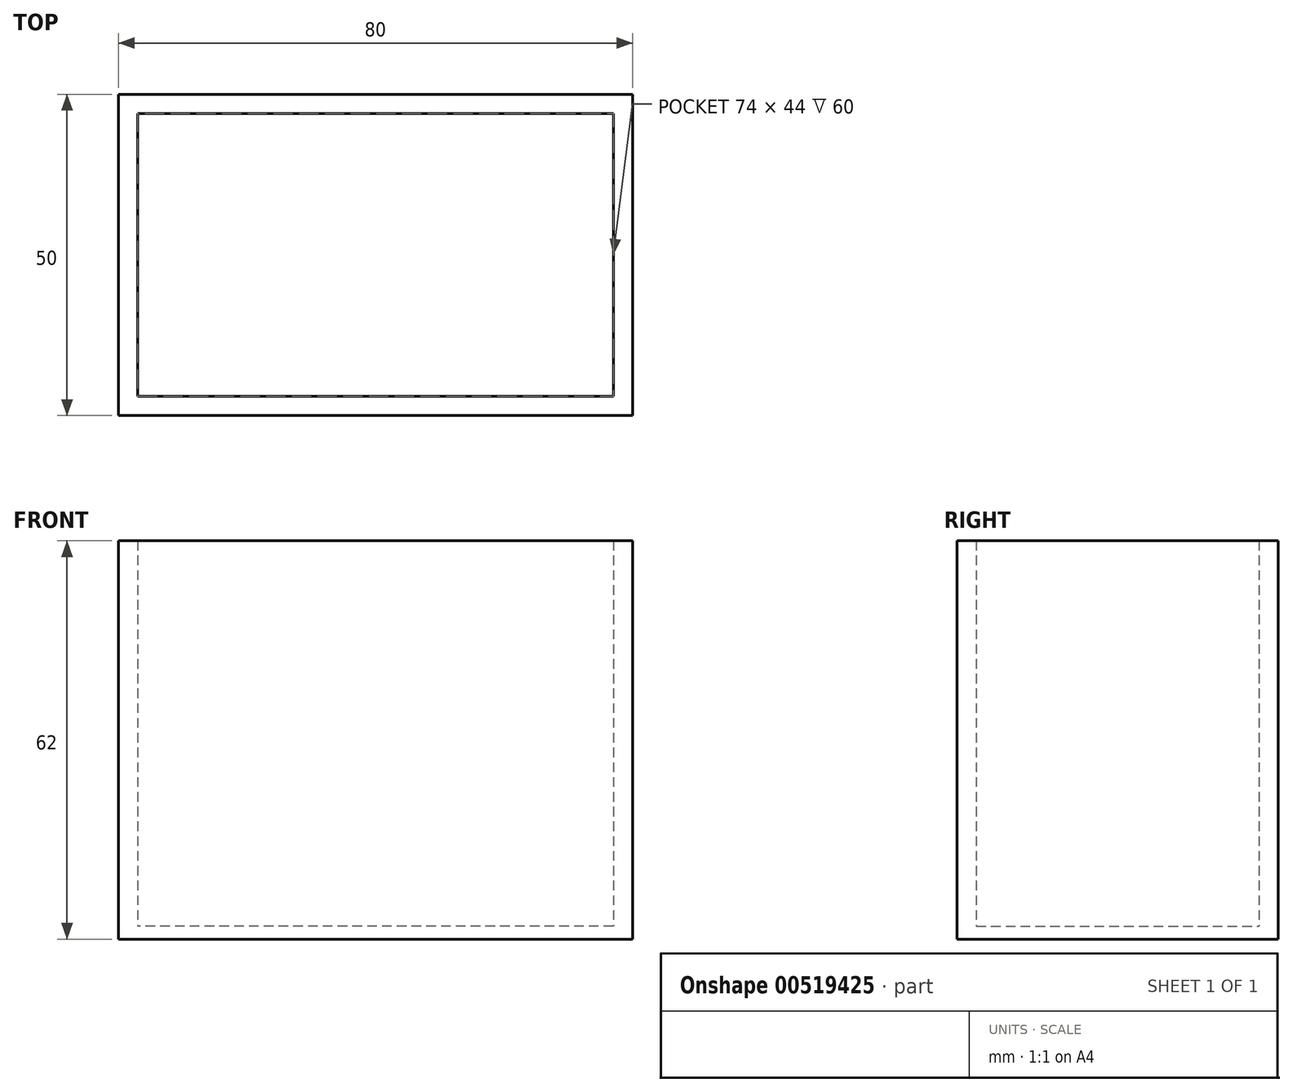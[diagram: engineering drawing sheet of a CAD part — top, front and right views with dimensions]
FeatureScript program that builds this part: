
annotation { "Feature Type Name" : "Feature", "Feature Type Description" : "" }
export const myFeature = defineFeature(function(context is Context, id is Id, definition is map)
    precondition{}
    {
        {
            var Q0;
            Q0=qCreatedBy(makeId("Top.planeOp"),FACE);
            var sketch = newSketch(context, id + "F0", { "sketchPlane" : qUnion([Q0])});
            skLineSegment(sketch, "E0.bottom", {"start": v(40, -25) * mm, "end": v(-40, -25) * mm});
            skLineSegment(sketch, "E0.top", {"start": v(40, 25) * mm, "end": v(-40, 25) * mm});
            skLineSegment(sketch, "E0.left", {"start": v(40, -25) * mm, "end": v(40, 25) * mm});
            skLineSegment(sketch, "E0.right", {"start": v(-40, -25) * mm, "end": v(-40, 25) * mm});
            skPoint(sketch, "E0.middle", {"position": v(0, 0) * mm});
            skSolve(sketch);
        }
        {
            var Q0;
            Q0 = qSketchRegion(id + "F0", true);
            var Q1;
            Q1=makeQuery(id+"F0.imprint","IMPRINT",FACE,{"disambiguationData":[TD([[makeQuery(id+"F0.imprint","IMPRINT",EDGE,{"derivedFrom":sQuery(id+"F0.wireOp",EDGE,"E0.bottom")}),-1.0]])]});
            extrude(context, id + "F1", {"entities" : qUnion([Q0, Q1]), "depth" : 2 * mm, "offsetDistance" : 25 * mm});
        }
        {
            var Q0;
            Q0=makeQuery(id+"F1.opExtrude","CAP_FACE",FACE,{"disambiguationData":[OSD([sQuery(id+"F0.wireOp",EDGE,"E0.bottom"),sQuery(id+"F0.wireOp",EDGE,"E0.top"),sQuery(id+"F0.wireOp",EDGE,"E0.left"),sQuery(id+"F0.wireOp",EDGE,"E0.right")])],"isStart":false});
            var sketch = newSketch(context, id + "F2", { "sketchPlane" : qUnion([Q0])});
            skLineSegment(sketch, "E1.bottom", {"start": v(37, -22) * mm, "end": v(-37, -22) * mm});
            skLineSegment(sketch, "E1.top", {"start": v(37, 22) * mm, "end": v(-37, 22) * mm});
            skLineSegment(sketch, "E1.left", {"start": v(37, -22) * mm, "end": v(37, 22) * mm});
            skLineSegment(sketch, "E1.right", {"start": v(-37, -22) * mm, "end": v(-37, 22) * mm});
            skPoint(sketch, "E1.middle", {"position": v(0, 0) * mm});
            skLineSegment(sketch, "E2.bottom", {"start": v(-40, 25) * mm, "end": v(40, 25) * mm});
            skLineSegment(sketch, "E2.top", {"start": v(-40, -25) * mm, "end": v(40, -25) * mm});
            skLineSegment(sketch, "E2.left", {"start": v(-40, 25) * mm, "end": v(-40, -25) * mm});
            skLineSegment(sketch, "E2.right", {"start": v(40, 25) * mm, "end": v(40, -25) * mm});
            skSolve(sketch);
        }
        {
            var Q0;
            Q0 = qSketchRegion(id + "F2", true);
            extrude(context, id + "F3", {"entities" : qUnion([Q0]), "operationType" : NewBodyOperationType.ADD, "depth" : 60 * mm, "offsetDistance" : 25 * mm});
        }
    });
